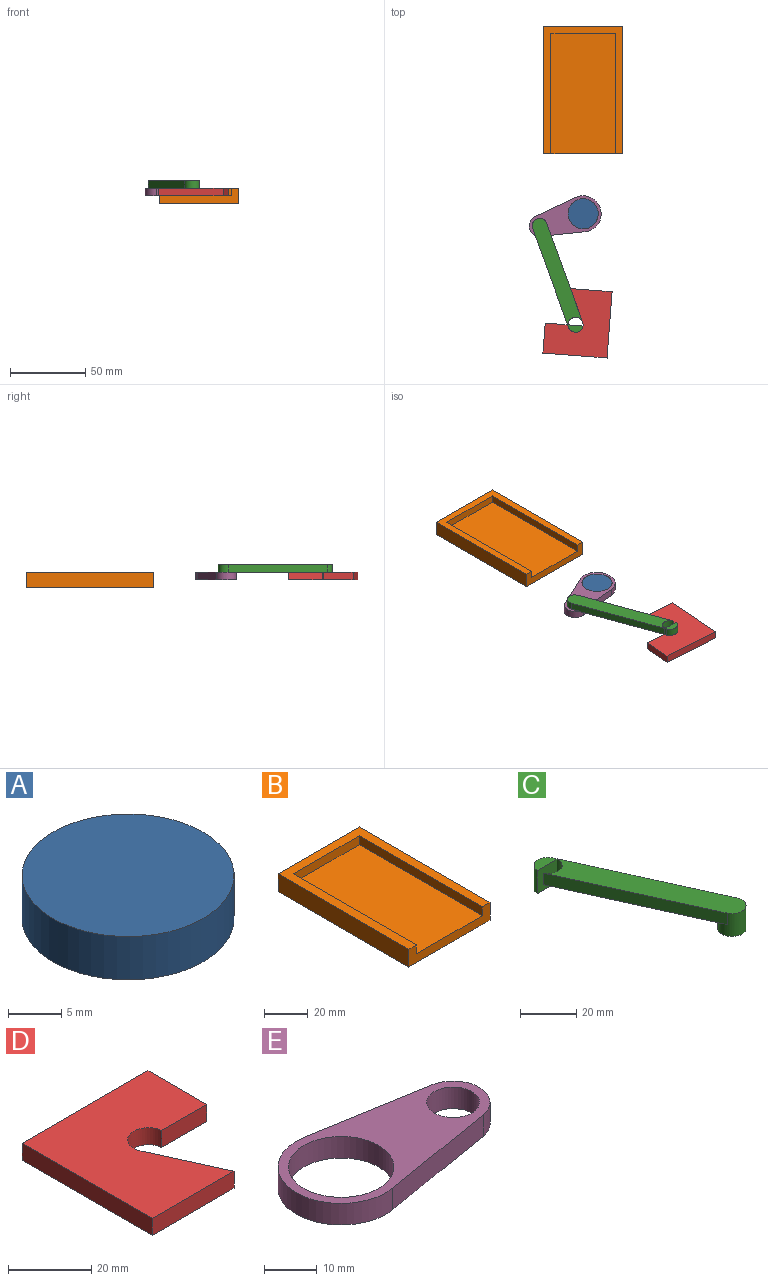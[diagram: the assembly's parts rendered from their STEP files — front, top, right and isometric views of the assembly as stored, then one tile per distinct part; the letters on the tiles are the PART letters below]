
ASSEMBLY  parts=5 mates=4
PART A: 3 faces, bbox 20x20x5 mm
  f0: cylinder r=10mm len=20mm, axis (0,0,-1), area 314.2mm2, adj f1,f2
  f1: plane 20x20mm, normal (0,0,1), area 314.2mm2, adj f0
  f2: plane 20x20mm, normal (0,0,-1), area 314.2mm2, adj f0
PART B: 10 faces, bbox 52.8x85x10 mm
  f0: plane 80x5mm, normal (-1,0,0), area 400mm2, adj f4,f6,f7,f9
  f1: plane 85x10mm, normal (1,0,0), area 850mm2, adj f2,f4,f7,f8
  f2: plane 52.8x10mm, normal (0,1,0), area 528mm2, adj f1,f3,f7,f8
  f3: plane 85x10mm, normal (-1,0,0), area 850mm2, adj f2,f4,f7,f8
  f4: plane 52.8x10mm, normal (0,-1,0), area 314mm2, adj f0,f1,f3,f5,f7,f8,f9
  f5: plane 80x5mm, normal (1,0,0), area 400mm2, adj f4,f6,f7,f9
  f6: plane 42.8x5mm, normal (0,-1,0), area 214mm2, adj f0,f5,f7,f9
  f7: plane 85x52.8mm, normal (0,0,1), area 1064mm2, adj f0,f1,f2,f3,f4,f5,f6
  f8: plane 85x52.8mm, normal (0,0,-1), area 4488.1mm2, adj f1,f2,f3,f4
  f9: plane 80x42.8mm, normal (0,0,1), area 3424.1mm2, adj f0,f4,f5,f6
PART C: 10 faces, bbox 38.9x73.8x10 mm
  f0: plane 67.89x37.99mm, normal (0,0,-1), area 621.5mm2, adj f1,f2,f3,f4,f6
  f1: plane 63.77x28.88mm, normal (-0.91,-0.41,0), area 350mm2, adj f0,f2,f6,f7
  f2: cylinder r=5mm len=10mm, axis (0,0,-1), area 235.6mm2, adj f0,f1,f3,f7,f8
  f3: plane 63.77x28.88mm, normal (0.91,0.41,0), area 350mm2, adj f0,f2,f4,f7
  f4: cylinder r=5mm len=10mm, axis (0,0,-1), area 139.7mm2, adj f0,f3,f5,f7,f9
  f5: plane 10x9.96mm, normal (0,-1,0), area 99.6mm2, adj f4,f6,f7,f9
  f6: cylinder r=5mm len=9.55mm, axis (0,0,-1), area 70.2mm2, adj f0,f1,f5,f7
  f7: plane 73.77x38.86mm, normal (0,0,1), area 734.8mm2, adj f1,f2,f3,f4,f5,f6
  f8: plane 10x10mm, normal (0,0,-1), area 78.5mm2, adj f2
  f9: plane 9.96x4.55mm, normal (0,0,-1), area 34.8mm2, adj f4,f5
PART D: 9 faces, bbox 42.8x44.2x5 mm
  f0: cylinder r=5mm len=9.98mm, axis (0,0,-1), area 86.9mm2, adj f1,f6,f7,f8
  f1: plane 15.3x5mm, normal (0,-1,0), area 76.5mm2, adj f0,f2,f7,f8
  f2: plane 20x5mm, normal (1,0,0), area 100mm2, adj f1,f3,f7,f8
  f3: plane 42.8x5mm, normal (0,1,0), area 214mm2, adj f2,f4,f7,f8
  f4: plane 44.22x5mm, normal (-1,0,0), area 221.1mm2, adj f3,f5,f7,f8
  f5: plane 27.8x5mm, normal (0,-1,0), area 139mm2, adj f4,f6,f7,f8
  f6: plane 21.7x9.83mm, normal (0.91,0.41,0), area 119.1mm2, adj f0,f5,f7,f8
  f7: plane 44.22x42.8mm, normal (0,0,1), area 1362.2mm2, adj f0,f1,f2,f3,f4,f5,f6
  f8: plane 44.22x42.8mm, normal (0,0,-1), area 1362.2mm2, adj f0,f1,f2,f3,f4,f5,f6
PART E: 8 faces, bbox 49x24x5 mm
  f0: cylinder r=12mm len=24mm, axis (0,0,-1), area 208.6mm2, adj f1,f3,f6,f7
  f1: plane 29.17x5mm, normal (0.17,-0.99,0), area 147.9mm2, adj f0,f2,f6,f7
  f2: cylinder r=7mm len=13.8mm, axis (0,0,-1), area 98.2mm2, adj f1,f3,f6,f7
  f3: plane 29.17x5mm, normal (0.17,0.99,0), area 147.9mm2, adj f0,f2,f6,f7
  f4: cylinder r=10mm len=20mm, axis (0,0,-1), area 314.2mm2, adj f6,f7
  f5: cylinder r=5mm len=10mm, axis (0,0,-1), area 157.1mm2, adj f6,f7
  f6: plane 49x24mm, normal (0,0,1), area 488.4mm2, adj f0,f1,f2,f3,f4,f5
  f7: plane 49x24mm, normal (0,0,-1), area 488.4mm2, adj f0,f1,f2,f3,f4,f5
PLACE A at identity fixed
PLACE B at identity fixed
PLACE C rot(axis=(0,0,1),175.6deg) t=(1.01,-10.33,0)mm
PLACE D rot(axis=(0,0,1),175.6deg) t=(1.01,-10.33,0)mm
PLACE E rot(axis=(0,0,-1),164.5deg) t=(0,0,0)mm
MATE pin_slot D.f8 <-> B.f9  axis (0,0,-1) through (0,-75.7,0)mm
MATE revolute D.f0 <-> C.f4  axis (0,0,-1) through (-5,-73.82,0)mm
MATE revolute A.f0 <-> E.f4  axis (0,0,-1) through (0,0,5)mm
MATE revolute C.f2 <-> E.f5  axis (0,0,-1) through (-28.91,-8.03,0)mm
